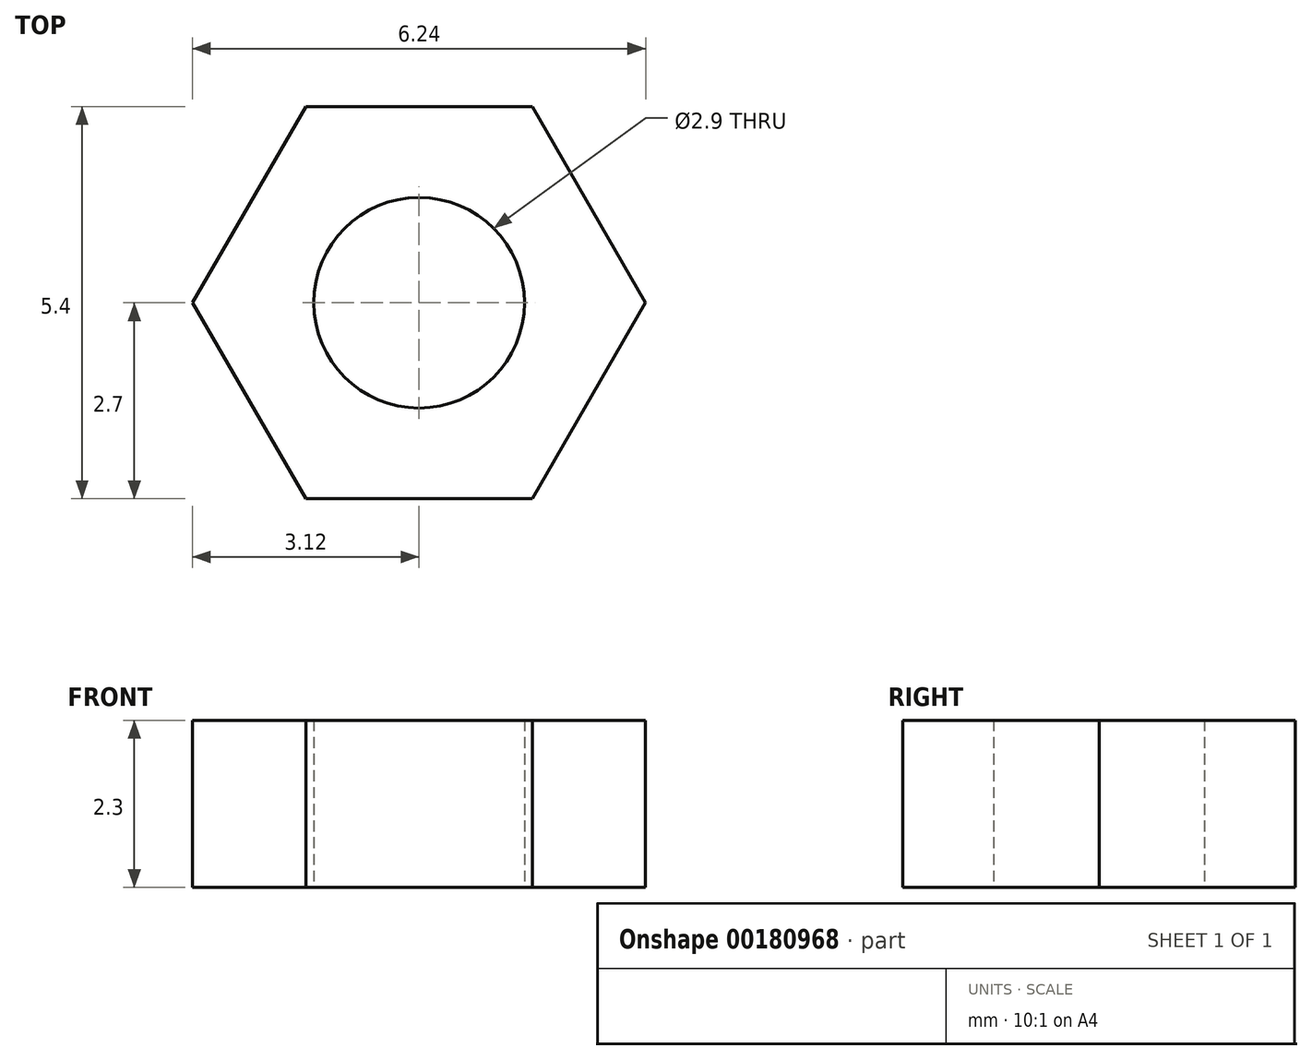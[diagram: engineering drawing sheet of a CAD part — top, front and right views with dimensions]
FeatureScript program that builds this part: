
annotation { "Feature Type Name" : "Feature", "Feature Type Description" : "" }
export const myFeature = defineFeature(function(context is Context, id is Id, definition is map)
    precondition{}
    {
        {
            var Q0;
            Q0=qCreatedBy(makeId("Top.planeOp"),FACE);
            var sketch = newSketch(context, id + "F0", { "sketchPlane" : qUnion([Q0])});
            skCircle(sketch, "E0.cCircle", {"center": v(0, 0) * mm, "radius": 2.7 * mm, "construction": true});
            skLineSegment(sketch, "E0.0", {"start": v(-1.56, 2.7) * mm, "end": v(1.56, 2.7) * mm});
            skLineSegment(sketch, "E0.1", {"start": v(1.56, 2.7) * mm, "end": v(3.12, 0) * mm});
            skLineSegment(sketch, "E0.2", {"start": v(3.12, 0) * mm, "end": v(1.56, -2.7) * mm});
            skLineSegment(sketch, "E0.3", {"start": v(1.56, -2.7) * mm, "end": v(-1.56, -2.7) * mm});
            skLineSegment(sketch, "E0.4", {"start": v(-1.56, -2.7) * mm, "end": v(-3.12, 0) * mm});
            skLineSegment(sketch, "E0.5", {"start": v(-3.12, 0) * mm, "end": v(-1.56, 2.7) * mm});
            skPoint(sketch, "E0.0.midPoint", {"position": v(0, 2.7) * mm});
            skCircle(sketch, "E1", {"center": v(0, 0) * mm, "radius": 1.45 * mm});
            skSolve(sketch);
        }
        {
            var Q0;
            Q0=qSketchRegion(id+"F0",true);
            extrude(context, id + "F1", {"entities" : qUnion([Q0]), "depth" : 2.3 * mm});
        }
    });
